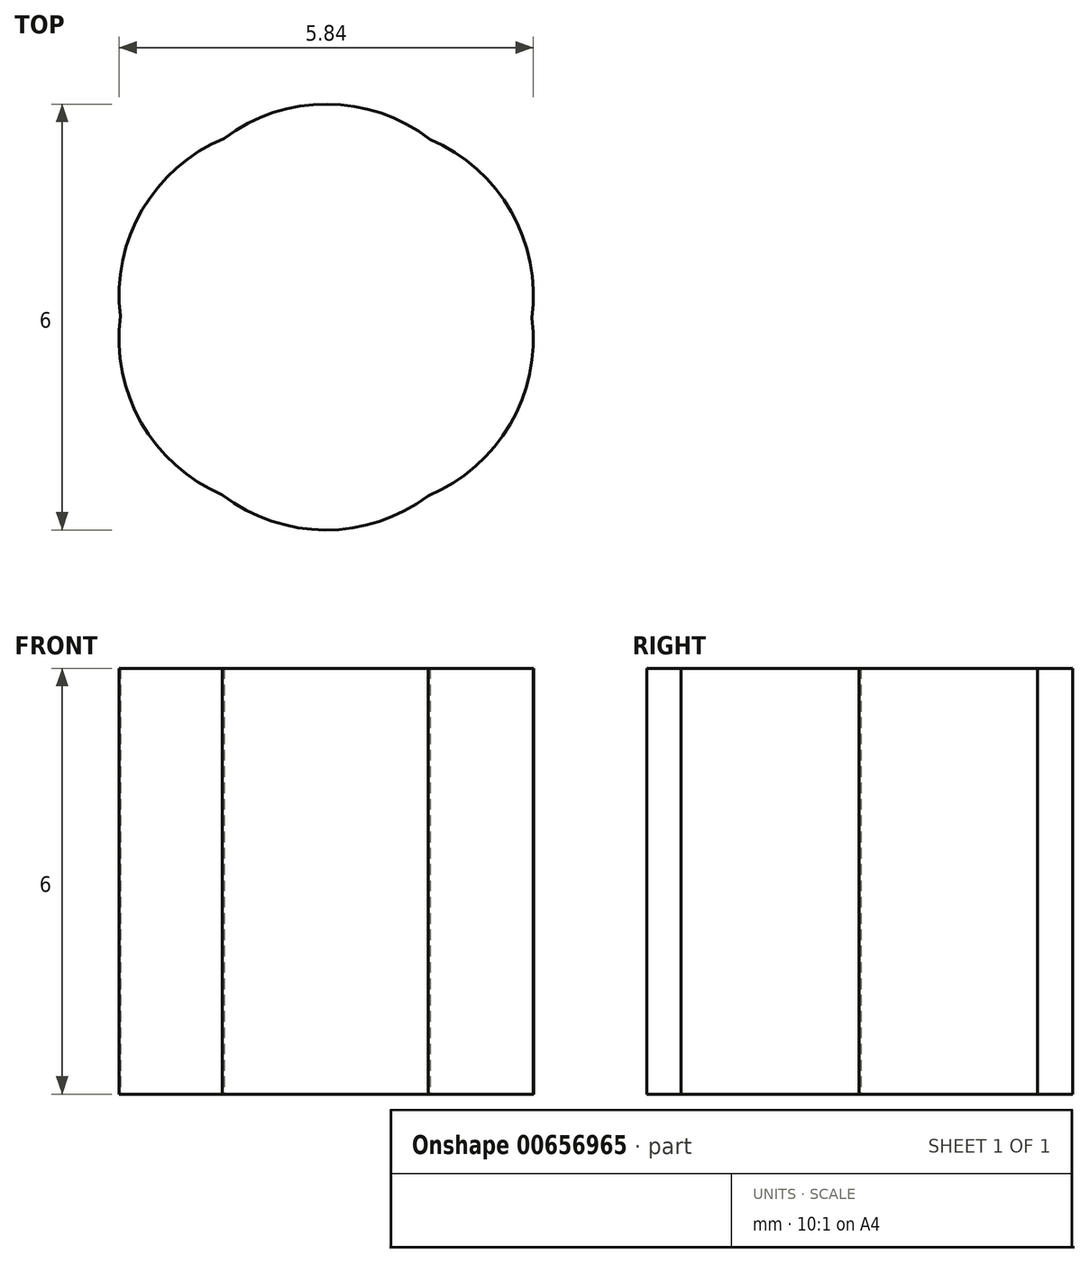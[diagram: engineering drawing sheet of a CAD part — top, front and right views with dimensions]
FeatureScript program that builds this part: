
annotation { "Feature Type Name" : "Feature", "Feature Type Description" : "" }
export const myFeature = defineFeature(function(context is Context, id is Id, definition is map)
    precondition{}
    {
        {
            var Q0;
            Q0=qCreatedBy(makeId("Top.planeOp"),FACE);
            var sketch = newSketch(context, id + "F0", { "sketchPlane" : qUnion([Q0])});
            skPoint(sketch, "E0.0.midPoint", {"position": v(1.5, 2.58) * mm});
            skArc(sketch, "E1", {"start": v(1.46, 2.5) * mm, "mid": v(0.01, 3) * mm, "end": v(-1.44, 2.52) * mm});
            skArc(sketch, "E2.trimOffspring", {"start": v(2.9, -0.01) * mm, "mid": v(2.6, 1.49) * mm, "end": v(1.46, 2.5) * mm});
            skArc(sketch, "E3", {"start": v(-1.46, -2.5) * mm, "mid": v(-0.01, -3) * mm, "end": v(1.44, -2.52) * mm});
            skArc(sketch, "E4", {"start": v(-2.9, 0.01) * mm, "mid": v(-2.6, -1.49) * mm, "end": v(-1.46, -2.5) * mm});
            skArc(sketch, "E5", {"start": v(-1.44, 2.52) * mm, "mid": v(-2.6, 1.51) * mm, "end": v(-2.9, 0.01) * mm});
            skArc(sketch, "E6.trimOffspring", {"start": v(1.44, -2.52) * mm, "mid": v(2.6, -1.51) * mm, "end": v(2.9, -0.01) * mm});
            skSolve(sketch);
        }
        {
            var Q0;
            Q0 = qSketchRegion(id + "F0", true);
            extrude(context, id + "F1", {"entities" : qUnion([Q0]), "depth" : 6 * mm, "offsetDistance" : 25 * mm});
        }
    });
